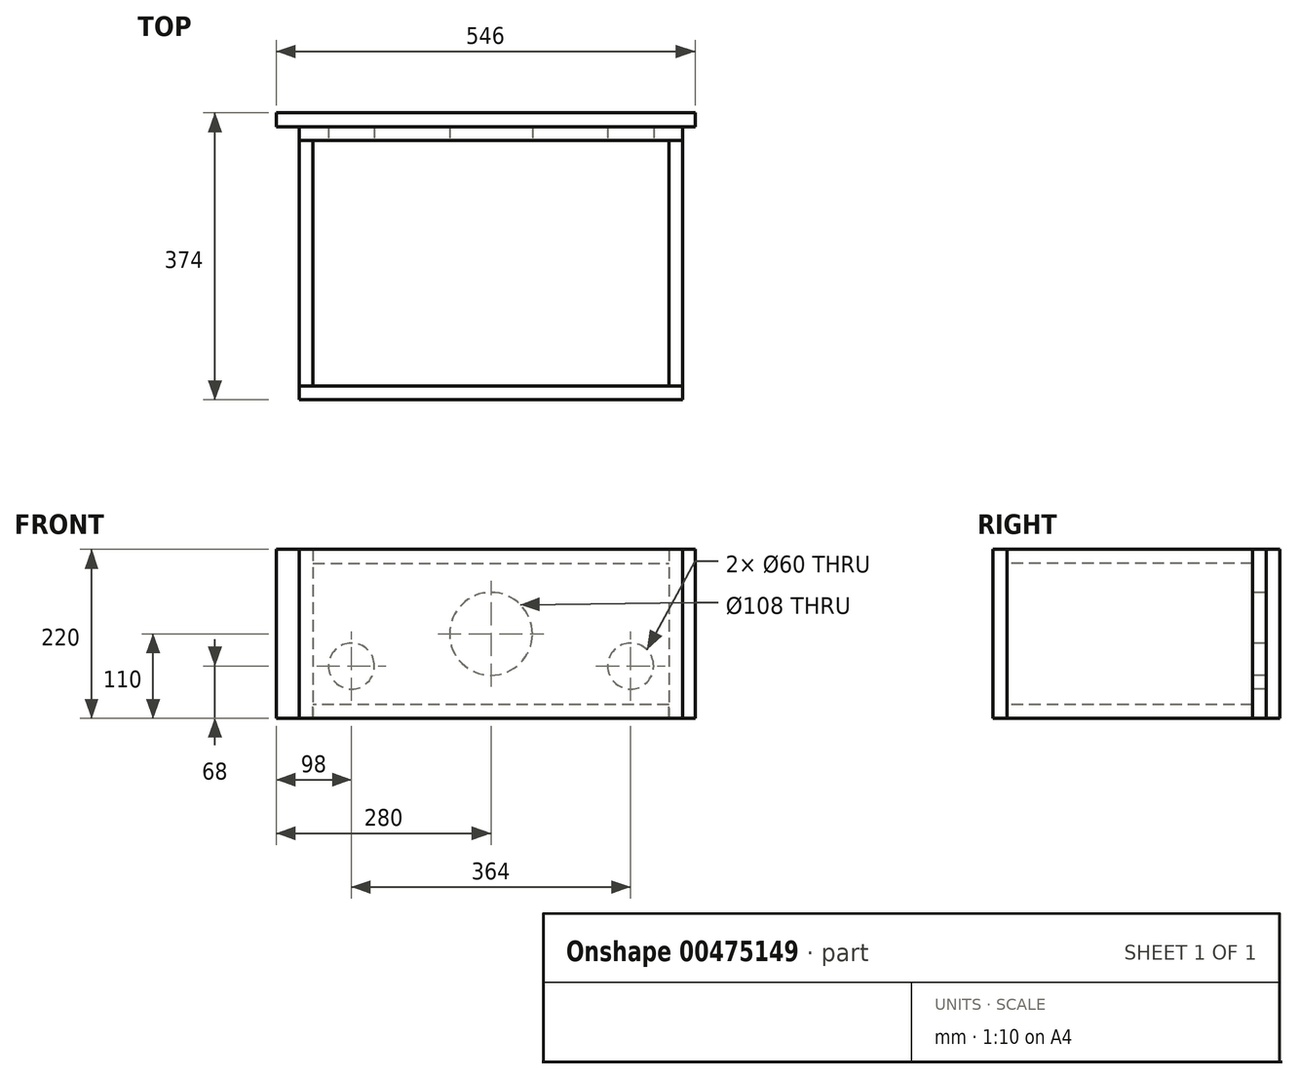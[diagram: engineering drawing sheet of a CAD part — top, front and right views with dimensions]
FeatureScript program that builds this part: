
annotation { "Feature Type Name" : "Feature", "Feature Type Description" : "" }
export const myFeature = defineFeature(function(context is Context, id is Id, definition is map)
    precondition{}
    {
        {
            var Q0;
            Q0=qCreatedBy(makeId("Front.planeOp"),FACE);
            var sketch = newSketch(context, id + "F0", { "sketchPlane" : qUnion([Q0])});
            skLineSegment(sketch, "E0.bottom", {"start": v(250, -110) * mm, "end": v(-250, -110) * mm});
            skLineSegment(sketch, "E0.top", {"start": v(250, 110) * mm, "end": v(-250, 110) * mm});
            skLineSegment(sketch, "E0.left", {"start": v(250, -110) * mm, "end": v(250, 110) * mm});
            skLineSegment(sketch, "E0.right", {"start": v(-250, -110) * mm, "end": v(-250, 110) * mm});
            skPoint(sketch, "E0.middle", {"position": v(0, 0) * mm});
            skSolve(sketch);
        }
        {
            var Q0;
            Q0=qSketchRegion(id+"F0",true);
            extrude(context, id + "F1", {"entities" : qUnion([Q0]), "depth" : 18 * mm});
        }
        {
            var Q0;
            Q0=makeQuery(id+"F1.opExtrude","CAP_FACE",FACE,{"disambiguationData":[OSD([sQuery(id+"F0.wireOp",EDGE,"E0.bottom"),sQuery(id+"F0.wireOp",EDGE,"E0.top"),sQuery(id+"F0.wireOp",EDGE,"E0.left"),sQuery(id+"F0.wireOp",EDGE,"E0.right")])],"isStart":true});
            var sketch = newSketch(context, id + "F2", { "sketchPlane" : qUnion([Q0])});
            skLineSegment(sketch, "E1.bottom", {"start": v(-250, 110) * mm, "end": v(-232, 110) * mm});
            skLineSegment(sketch, "E1.top", {"start": v(-250, -110) * mm, "end": v(-232, -110) * mm});
            skLineSegment(sketch, "E1.left", {"start": v(-250, 110) * mm, "end": v(-250, -110) * mm});
            skLineSegment(sketch, "E1.right", {"start": v(-232, 110) * mm, "end": v(-232, -110) * mm});
            skSolve(sketch);
        }
        {
            var Q0;
            Q0=qSketchRegion(id+"F2",true);
            extrude(context, id + "F3", {"entities" : qUnion([Q0]), "depth" : 320 * mm});
        }
        {
            var Q0;
            Q0=makeQuery(id+"F1.opExtrude","CAP_FACE",FACE,{"disambiguationData":[OSD([sQuery(id+"F0.wireOp",EDGE,"E0.bottom"),sQuery(id+"F0.wireOp",EDGE,"E0.top"),sQuery(id+"F0.wireOp",EDGE,"E0.left"),sQuery(id+"F0.wireOp",EDGE,"E0.right")])],"isStart":true});
            var sketch = newSketch(context, id + "F4", { "sketchPlane" : qUnion([Q0])});
            skLineSegment(sketch, "E2.bottom", {"start": v(250, 110) * mm, "end": v(232, 110) * mm});
            skLineSegment(sketch, "E2.top", {"start": v(250, -110) * mm, "end": v(232, -110) * mm});
            skLineSegment(sketch, "E2.left", {"start": v(250, 110) * mm, "end": v(250, -110) * mm});
            skLineSegment(sketch, "E2.right", {"start": v(232, 110) * mm, "end": v(232, -110) * mm});
            skSolve(sketch);
        }
        {
            var Q0;
            Q0=qSketchRegion(id+"F4",true);
            extrude(context, id + "F5", {"entities" : qUnion([Q0]), "depth" : 320 * mm});
        }
        {
            var Q0;
            Q0=makeQuery(id+"F1.opExtrude","CAP_FACE",FACE,{"disambiguationData":[OSD([sQuery(id+"F0.wireOp",EDGE,"E0.bottom"),sQuery(id+"F0.wireOp",EDGE,"E0.top"),sQuery(id+"F0.wireOp",EDGE,"E0.left"),sQuery(id+"F0.wireOp",EDGE,"E0.right")])],"isStart":true});
            var sketch = newSketch(context, id + "F6", { "sketchPlane" : qUnion([Q0])});
            skLineSegment(sketch, "E3.bottom", {"start": v(232, 110) * mm, "end": v(-232, 110) * mm});
            skLineSegment(sketch, "E3.top", {"start": v(232, 92) * mm, "end": v(-232, 92) * mm});
            skLineSegment(sketch, "E3.left", {"start": v(232, 110) * mm, "end": v(232, 92) * mm});
            skLineSegment(sketch, "E3.right", {"start": v(-232, 110) * mm, "end": v(-232, 92) * mm});
            skSolve(sketch);
        }
        {
            var Q0;
            Q0=makeQuery(id+"F6.imprint","IMPRINT",FACE,{"disambiguationData":[TD([[makeQuery(id+"F6.imprint","IMPRINT",EDGE,{"derivedFrom":sQuery(id+"F6.wireOp",EDGE,"E3.top")}),1.0]])]});
            var sketch = newSketch(context, id + "F7", { "sketchPlane" : qUnion([Q0])});
            skLineSegment(sketch, "E4.bottom", {"start": v(-232, -110) * mm, "end": v(232, -110) * mm});
            skLineSegment(sketch, "E4.top", {"start": v(-232, -92) * mm, "end": v(232, -92) * mm});
            skLineSegment(sketch, "E4.left", {"start": v(-232, -110) * mm, "end": v(-232, -92) * mm});
            skLineSegment(sketch, "E4.right", {"start": v(232, -110) * mm, "end": v(232, -92) * mm});
            skSolve(sketch);
        }
        {
            var Q0;
            Q0=qSketchRegion(id+"F6",true);
            extrude(context, id + "F8", {"entities" : qUnion([Q0]), "depth" : 320 * mm});
        }
        {
            var Q0;
            Q0=qSketchRegion(id+"F7",true);
            extrude(context, id + "F9", {"entities" : qUnion([Q0]), "depth" : 320 * mm});
        }
        {
            var Q0;
            Q0=makeQuery(id+"F8.opExtrude","CAP_FACE",FACE,{"disambiguationData":[OSD([sQuery(id+"F6.wireOp",EDGE,"E3.bottom"),sQuery(id+"F6.wireOp",EDGE,"E3.top"),sQuery(id+"F6.wireOp",EDGE,"E3.left"),sQuery(id+"F6.wireOp",EDGE,"E3.right")])],"isStart":false});
            var sketch = newSketch(context, id + "F10", { "sketchPlane" : qUnion([Q0])});
            skLineSegment(sketch, "E5.bottom", {"start": v(-250, 110) * mm, "end": v(250, 110) * mm});
            skLineSegment(sketch, "E5.top", {"start": v(-250, -110) * mm, "end": v(250, -110) * mm});
            skLineSegment(sketch, "E5.left", {"start": v(-250, 110) * mm, "end": v(-250, -110) * mm});
            skLineSegment(sketch, "E5.right", {"start": v(250, 110) * mm, "end": v(250, -110) * mm});
            skCircle(sketch, "E6", {"center": v(0, 0) * mm, "radius": 54 * mm});
            skCircle(sketch, "E7", {"center": v(-182, -42) * mm, "radius": 30 * mm});
            skCircle(sketch, "E8", {"center": v(182, -42) * mm, "radius": 30 * mm});
            skSolve(sketch);
        }
        {
            var Q0;
            Q0=qSketchRegion(id+"F10",true);
            extrude(context, id + "F11", {"entities" : qUnion([Q0]), "depth" : 18 * mm});
        }
        {
            var Q0;
            Q0=makeQuery(id+"F11.opExtrude","SWEPT_BODY",BODY,{"disambiguationData":[OSD([sQuery(id+"F10.wireOp",EDGE,"E5.bottom"),sQuery(id+"F10.wireOp",EDGE,"E5.top"),sQuery(id+"F10.wireOp",EDGE,"E5.left"),sQuery(id+"F10.wireOp",EDGE,"E5.right"),sQuery(id+"F10.wireOp",EDGE,"E6")])]});
            transform(context, id + "F12", {"entities" : qUnion([Q0]), "transformType" : TransformType.TRANSLATION_3D, "dx" : 0 * mm, "dy" : 18 * mm, "dz" : 0 * mm, "makeCopy" : true});
        }
        {
            var Q0;
            Q0=makeQuery(id+"F12.opPattern","COPY",BODY,{"derivedFrom":makeQuery(id+"F11.opExtrude","SWEPT_BODY",BODY,{"disambiguationData":[OSD([sQuery(id+"F10.wireOp",EDGE,"E5.bottom"),sQuery(id+"F10.wireOp",EDGE,"E5.top"),sQuery(id+"F10.wireOp",EDGE,"E5.left"),sQuery(id+"F10.wireOp",EDGE,"E5.right"),sQuery(id+"F10.wireOp",EDGE,"E6")])]}),"instanceName":"1"});
            deleteBodies(context, id + "F13", {"entities" : qUnion([Q0])});
        }
        {
            var Q0;
            Q0=makeQuery(id+"F11.opExtrude","CAP_FACE",FACE,{"disambiguationData":[OSD([sQuery(id+"F10.wireOp",EDGE,"E5.bottom"),sQuery(id+"F10.wireOp",EDGE,"E5.top"),sQuery(id+"F10.wireOp",EDGE,"E5.left"),sQuery(id+"F10.wireOp",EDGE,"E5.right"),sQuery(id+"F10.wireOp",EDGE,"E6")])],"isStart":false});
            var sketch = newSketch(context, id + "F14", { "sketchPlane" : qUnion([Q0])});
            skLineSegment(sketch, "E9.bottom", {"start": v(-266, 110) * mm, "end": v(280, 110) * mm});
            skLineSegment(sketch, "E9.top", {"start": v(-266, -110) * mm, "end": v(280, -110) * mm});
            skLineSegment(sketch, "E9.left", {"start": v(-266, 110) * mm, "end": v(-266, -110) * mm});
            skLineSegment(sketch, "E9.right", {"start": v(280, 110) * mm, "end": v(280, -110) * mm});
            skSolve(sketch);
        }
        {
            var Q0;
            Q0=qSketchRegion(id+"F14",true);
            extrude(context, id + "F15", {"entities" : qUnion([Q0]), "depth" : 18 * mm});
        }
    });
